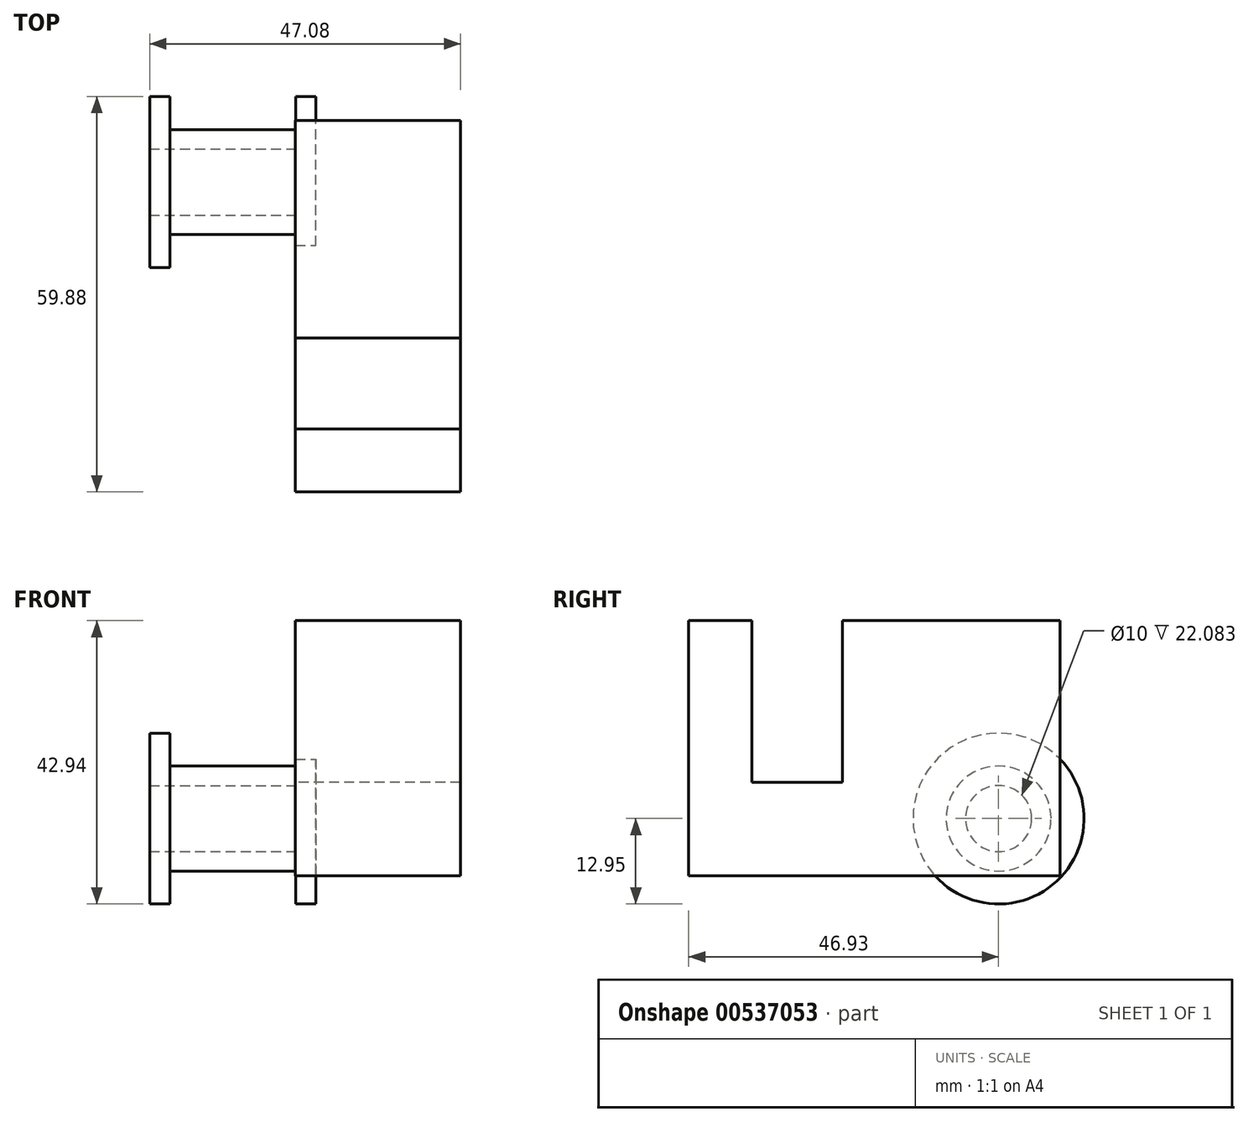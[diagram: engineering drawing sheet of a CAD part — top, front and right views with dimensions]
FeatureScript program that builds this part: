
annotation { "Feature Type Name" : "Feature", "Feature Type Description" : "" }
export const myFeature = defineFeature(function(context is Context, id is Id, definition is map)
    precondition{}
    {
        {
            var Q0;
            Q0=qCreatedBy(makeId("Front.planeOp"),FACE);
            var sketch = newSketch(context, id + "F0", { "sketchPlane" : qUnion([Q0])});
            skLineSegment(sketch, "E0", {"start": v(-22.08, 0) * mm, "end": v(-22.08, 12.95) * mm});
            skLineSegment(sketch, "E1", {"start": v(-22.08, 12.95) * mm, "end": v(-18.98, 12.95) * mm});
            skLineSegment(sketch, "E2", {"start": v(-18.98, 12.95) * mm, "end": v(-18.98, 7.95) * mm});
            skLineSegment(sketch, "E3", {"start": v(-18.98, 7.95) * mm, "end": v(0.02, 7.95) * mm});
            skLineSegment(sketch, "E4", {"start": v(0.02, 7.95) * mm, "end": v(0.02, 12.95) * mm});
            skLineSegment(sketch, "E5", {"start": v(0.02, 12.95) * mm, "end": v(3.12, 12.95) * mm});
            skLineSegment(sketch, "E6", {"start": v(3.12, 12.95) * mm, "end": v(3.12, 0) * mm});
            skLineSegment(sketch, "E7", {"start": v(16.27, 0) * mm, "end": v(-32.24, 0) * mm, "construction": true});
            skLineSegment(sketch, "E8", {"start": v(-22.08, 0) * mm, "end": v(3.12, 0) * mm});
            skSolve(sketch);
        }
        {
            var Q0;
            Q0 = qSketchRegion(id + "F0", true);
            var Q1;
            Q1=sQuery(id+"F0.wireOp",EDGE,"E7");
            revolve(context, id + "F1", {"entities" : qUnion([Q0]), "axis" : qUnion([Q1]), "revolveType" : RevolveType.FULL});
        }
        {
            var Q0;
            Q0=makeQuery(id+"F1.opRevolve","SWEPT_FACE",FACE,{"disambiguationData":[OSD([sQuery(id+"F0.wireOp",EDGE,"E6")])]});
            var sketch = newSketch(context, id + "F2", { "sketchPlane" : qUnion([Q0])});
            skCircle(sketch, "E9", {"center": v(0, 0) * mm, "radius": 5 * mm});
            skSolve(sketch);
        }
        {
            var Q0;
            Q0=makeQuery(id+"F2.imprint","IMPRINT",FACE,{"disambiguationData":[TD([[makeQuery(id+"F2.imprint","IMPRINT",EDGE,{"derivedFrom":sQuery(id+"F2.wireOp",EDGE,"E9")}),1.0]])]});
            extrude(context, id + "F3", {"entities" : qUnion([Q0]), "operationType" : NewBodyOperationType.REMOVE, "oppositeDirection" : true, "depth" : 30 * mm, "offsetDistance" : 25 * mm});
        }
        {
            var Q0;
            Q0=qCreatedBy(makeId("Right.planeOp"),FACE);
            var sketch = newSketch(context, id + "F4", { "sketchPlane" : qUnion([Q0])});
            skLineSegment(sketch, "E10.bottom", {"start": v(-46.93, 29.99) * mm, "end": v(9.33, 29.99) * mm});
            skLineSegment(sketch, "E10.top", {"start": v(-46.93, -8.69) * mm, "end": v(9.33, -8.69) * mm});
            skLineSegment(sketch, "E10.left", {"start": v(-46.93, 29.99) * mm, "end": v(-46.93, -8.69) * mm});
            skLineSegment(sketch, "E10.right", {"start": v(9.33, 29.99) * mm, "end": v(9.33, -8.69) * mm});
            skLineSegment(sketch, "E11.bottom", {"start": v(-37.38, 29.99) * mm, "end": v(-23.62, 29.99) * mm});
            skLineSegment(sketch, "E11.top", {"start": v(-37.38, 5.46) * mm, "end": v(-23.62, 5.46) * mm});
            skLineSegment(sketch, "E11.left", {"start": v(-37.38, 29.99) * mm, "end": v(-37.38, 5.46) * mm});
            skLineSegment(sketch, "E11.right", {"start": v(-23.62, 29.99) * mm, "end": v(-23.62, 5.46) * mm});
            skSolve(sketch);
        }
        {
            var Q0;
            Q0=makeQuery(id+"F4.imprint","IMPRINT",FACE,{"disambiguationData":[TD([[makeQuery(id+"F4.imprint","IMPRINT",EDGE,{"derivedFrom":sQuery(id+"F4.wireOp",EDGE,"E10.top")}),1.0]])]});
            extrude(context, id + "F5", {"entities" : qUnion([Q0]), "operationType" : NewBodyOperationType.ADD, "depth" : 25 * mm, "offsetDistance" : 25 * mm});
        }
    });
